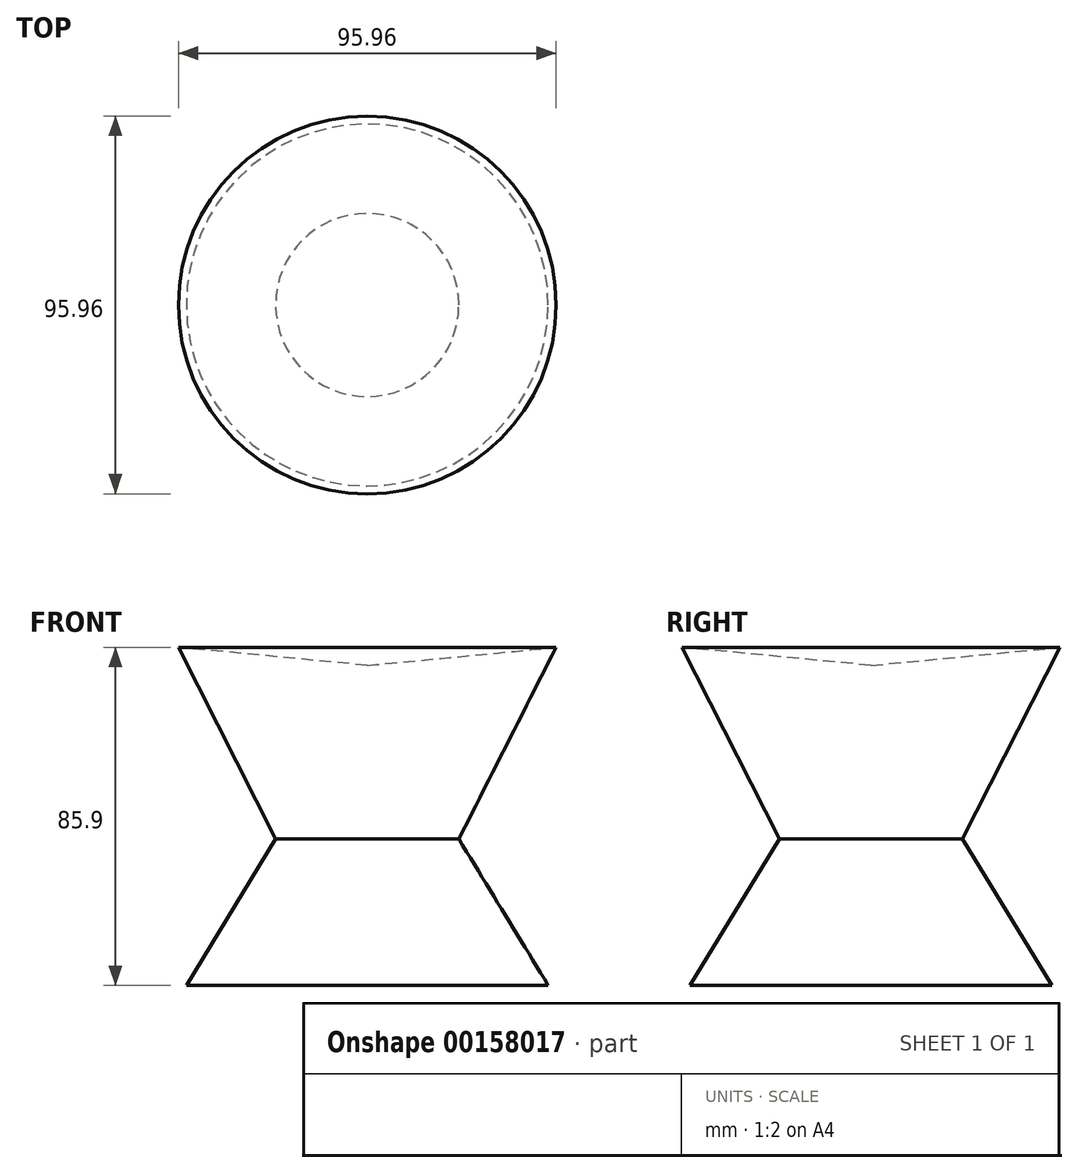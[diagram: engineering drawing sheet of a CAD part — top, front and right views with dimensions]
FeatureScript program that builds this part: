
annotation { "Feature Type Name" : "Feature", "Feature Type Description" : "" }
export const myFeature = defineFeature(function(context is Context, id is Id, definition is map)
    precondition{}
    {
        {
            var Q0;
            Q0=qCreatedBy(makeId("Front.planeOp"),FACE);
            var sketch = newSketch(context, id + "F0", { "sketchPlane" : qUnion([Q0])});
            skLineSegment(sketch, "E0", {"start": v(0, 44.1) * mm, "end": v(0, -37.2) * mm});
            skLineSegment(sketch, "E1", {"start": v(0, -37.2) * mm, "end": v(45.97, -37.2) * mm});
            skLineSegment(sketch, "E2", {"start": v(45.97, -37.2) * mm, "end": v(23.27, 0) * mm});
            skLineSegment(sketch, "E3", {"start": v(23.27, 0) * mm, "end": v(47.98, 48.7) * mm});
            skLineSegment(sketch, "E4", {"start": v(47.98, 48.7) * mm, "end": v(0, 44.1) * mm});
            skSolve(sketch);
        }
        {
            var Q0;
            Q0=makeQuery(id+"F0.imprint","IMPRINT",FACE,{"disambiguationData":[TD([[makeQuery(id+"F0.imprint","IMPRINT",EDGE,{"derivedFrom":sQuery(id+"F0.wireOp",EDGE,"E0")}),1.0]])]});
            var Q1;
            Q1=sQuery(id+"F0.wireOp",EDGE,"E0");
            revolve(context, id + "F1", {"entities" : qUnion([Q0]), "axis" : qUnion([Q1]), "revolveType" : RevolveType.FULL});
        }
    });
